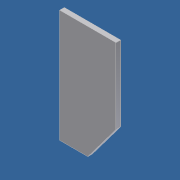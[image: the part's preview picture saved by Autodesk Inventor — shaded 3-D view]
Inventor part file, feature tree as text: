
AUTODESK INVENTOR PART (.ipt)
format: ipt  version: 2012 (Build 160160000, 160)  size: 68,096 bytes
history: native  units: in
note: dims shown in document units (in); Inventor stores cm internally (conversion verified against a paired STEP export)
features: extrude x1, sketch x1
ambient origin geometry x8: Origin, YZ Plane, XZ Plane, XY Plane, X Axis, Y Axis, Z Axis, Center Point
bodies: Solid1 (feature_tree)
feature tree (2):
  extrude  "Extrusion1"  Depth=3.0in
  sketch  "Sketch1"  dims[d2=0.25in d3=0.0in d4=3.0in d5=6.0in d6=4.0in d7=1.5in]
